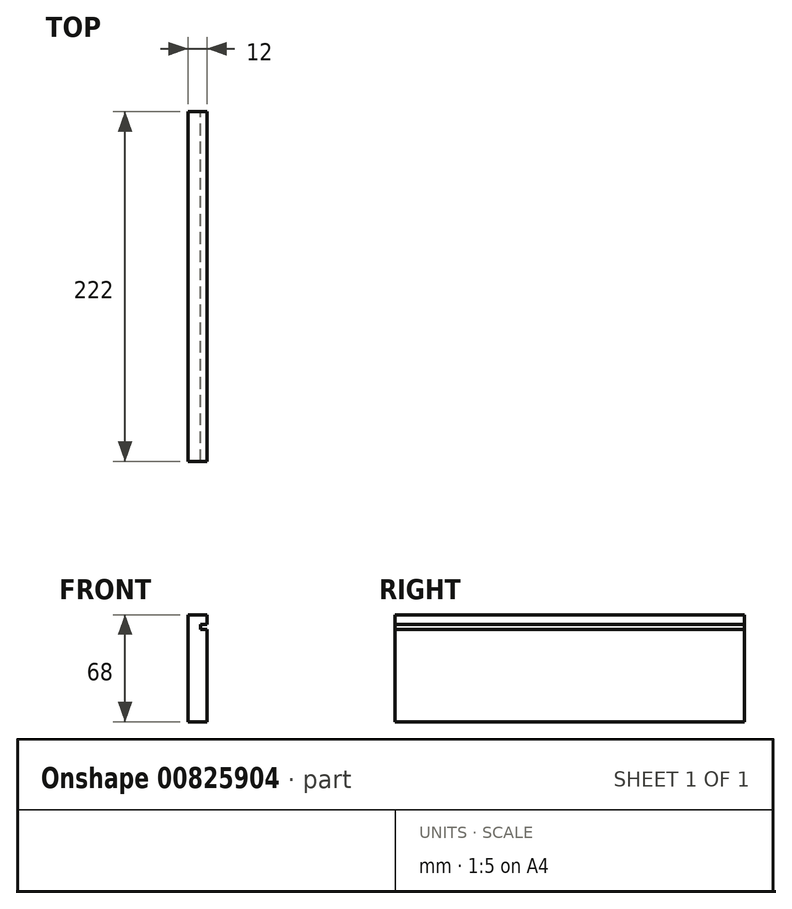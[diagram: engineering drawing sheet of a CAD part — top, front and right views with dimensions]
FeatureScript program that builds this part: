
annotation { "Feature Type Name" : "Feature", "Feature Type Description" : "" }
export const myFeature = defineFeature(function(context is Context, id is Id, definition is map)
    precondition{}
    {
        {
            var Q0;
            Q0=qCreatedBy(makeId("Right.planeOp"),FACE);
            var sketch = newSketch(context, id + "F0", { "sketchPlane" : qUnion([Q0])});
            skLineSegment(sketch, "E0.bottom", {"start": v(111, 34) * mm, "end": v(-111, 34) * mm});
            skLineSegment(sketch, "E0.top", {"start": v(111, -34) * mm, "end": v(-111, -34) * mm});
            skLineSegment(sketch, "E0.left", {"start": v(111, 34) * mm, "end": v(111, -34) * mm});
            skLineSegment(sketch, "E0.right", {"start": v(-111, 34) * mm, "end": v(-111, -34) * mm});
            skPoint(sketch, "E0.middle", {"position": v(0, 0) * mm});
            skSolve(sketch);
        }
        {
            var Q0;
            Q0 = qSketchRegion(id + "F0", true);
            extrude(context, id + "F1", {"entities" : qUnion([Q0]), "depth" : 12 * mm, "offsetDistance" : 25.4 * mm});
        }
        {
            var Q0;
            Q0=makeQuery(id+"F1.opExtrude","SWEPT_FACE",FACE,{"disambiguationData":[OSD([sQuery(id+"F0.wireOp",EDGE,"E0.left")])]});
            var sketch = newSketch(context, id + "F2", { "sketchPlane" : qUnion([Q0])});
            skLineSegment(sketch, "E1.bottom", {"start": v(-12, 27.73) * mm, "end": v(-8.05, 27.73) * mm});
            skLineSegment(sketch, "E1.top", {"start": v(-12, 24.73) * mm, "end": v(-8.05, 24.73) * mm});
            skLineSegment(sketch, "E1.left", {"start": v(-12, 27.73) * mm, "end": v(-12, 24.73) * mm});
            skLineSegment(sketch, "E1.right", {"start": v(-8.05, 27.73) * mm, "end": v(-8.05, 24.73) * mm});
            skPoint(sketch, "E1.middle", {"position": v(-10.03, 26.23) * mm});
            skSolve(sketch);
        }
        {
            var Q0;
            Q0 = qSketchRegion(id + "F2", true);
            extrude(context, id + "F3", {"entities" : qUnion([Q0]), "operationType" : NewBodyOperationType.REMOVE, "oppositeDirection" : true, "depth" : 300 * mm, "offsetDistance" : 25.4 * mm});
        }
    });
